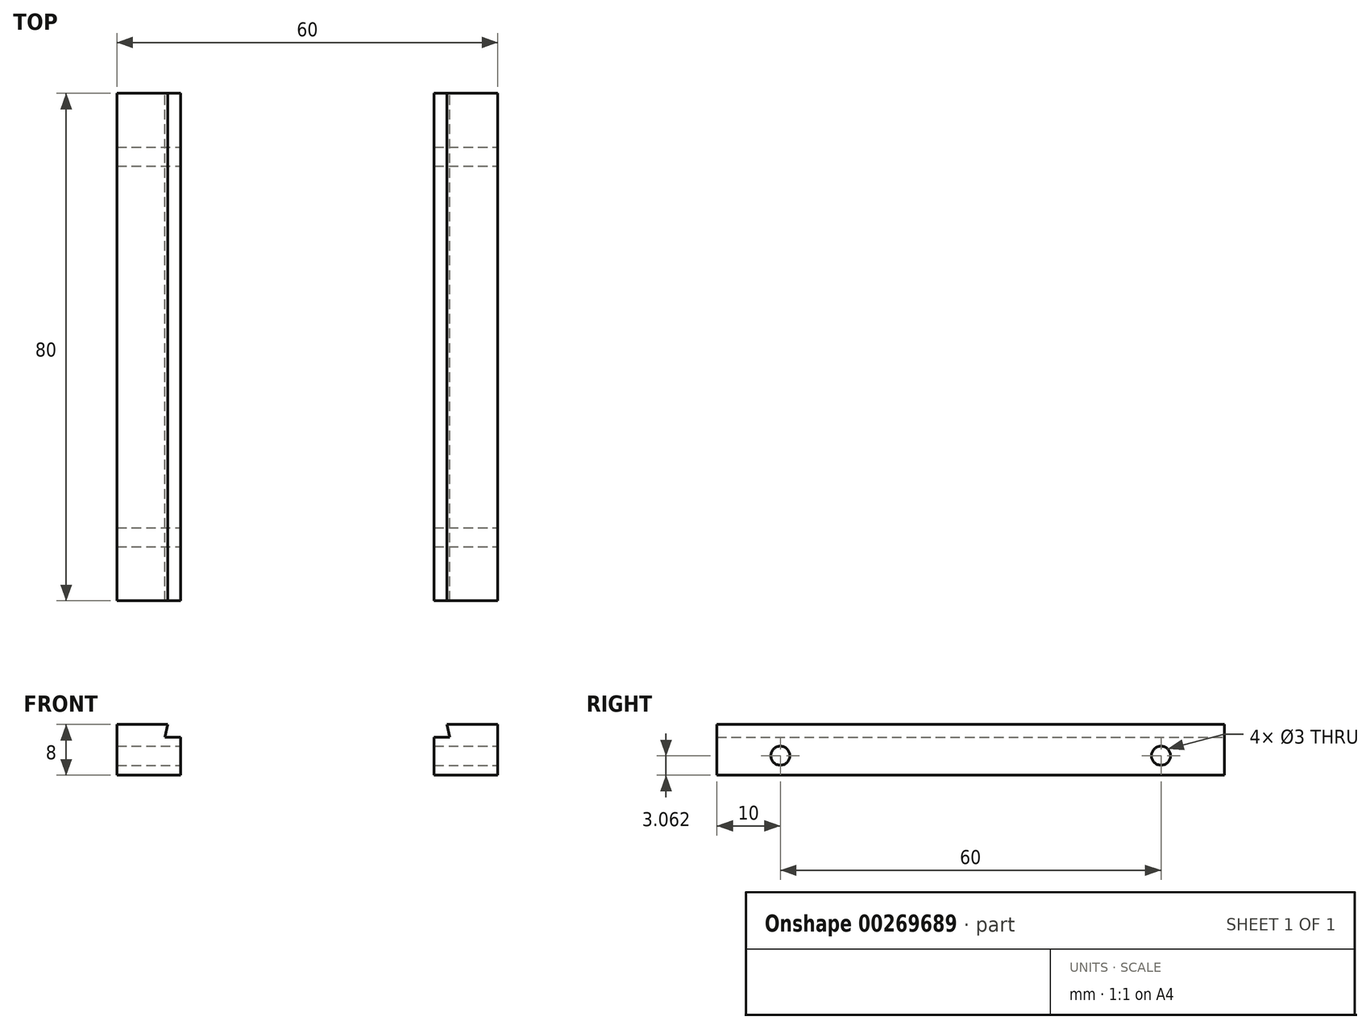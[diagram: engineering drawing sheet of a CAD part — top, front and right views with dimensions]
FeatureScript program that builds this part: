
annotation { "Feature Type Name" : "Feature", "Feature Type Description" : "" }
export const myFeature = defineFeature(function(context is Context, id is Id, definition is map)
    precondition{}
    {
        {
            var Q0;
            Q0=qCreatedBy(makeId("Front.planeOp"),FACE);
            var sketch = newSketch(context, id + "F0", { "sketchPlane" : qUnion([Q0])});
            skLineSegment(sketch, "E0.bottom", {"start": v(-30, 8) * mm, "end": v(-22, 8) * mm});
            skLineSegment(sketch, "E0.top", {"start": v(-30, 0) * mm, "end": v(-20, 0) * mm});
            skLineSegment(sketch, "E0.left", {"start": v(-30, 8) * mm, "end": v(-30, 0) * mm});
            skLineSegment(sketch, "E0.right", {"start": v(-20, 6) * mm, "end": v(-20, 0) * mm});
            skLineSegment(sketch, "E1", {"start": v(-22, 8) * mm, "end": v(-22.43, 6) * mm});
            skLineSegment(sketch, "E2", {"start": v(-22.43, 6) * mm, "end": v(-20, 6) * mm});
            skSolve(sketch);
        }
        {
            var Q0;
            Q0=makeQuery(id+"F0.imprint","IMPRINT",FACE,{"disambiguationData":[TD([[makeQuery(id+"F0.imprint","IMPRINT",EDGE,{"derivedFrom":sQuery(id+"F0.wireOp",EDGE,"E0.bottom")}),-1.0]])]});
            extrude(context, id + "F1", {"entities" : qUnion([Q0]), "depth" : 80 * mm});
        }
        {
            var Q0;
            Q0=makeQuery(id+"F1.opExtrude","SWEPT_BODY",BODY,{"disambiguationData":[OSD([sQuery(id+"F0.wireOp",EDGE,"E0.bottom"),sQuery(id+"F0.wireOp",EDGE,"E0.top"),sQuery(id+"F0.wireOp",EDGE,"E0.left"),sQuery(id+"F0.wireOp",EDGE,"E0.right"),sQuery(id+"F0.wireOp",EDGE,"E1"),sQuery(id+"F0.wireOp",EDGE,"E2")])]});
            var Q1;
            Q1=qCreatedBy(makeId("Right.planeOp"),FACE);
            mirror(context, id + "F2", {"entities" : qUnion([Q0]), "mirrorPlane" : qUnion([Q1])});
        }
        {
            var Q0;
            Q0=makeQuery(id+"F2.opPattern","COPY",FACE,{"derivedFrom":makeQuery(id+"F1.opExtrude","SWEPT_FACE",FACE,{"disambiguationData":[OSD([sQuery(id+"F0.wireOp",EDGE,"E0.left")])]}),"instanceName":"1"});
            var sketch = newSketch(context, id + "F3", { "sketchPlane" : qUnion([Q0])});
            skCircle(sketch, "E3", {"center": v(-70, 3.06) * mm, "radius": 1.5 * mm});
            skCircle(sketch, "E4", {"center": v(-10, 3.06) * mm, "radius": 1.5 * mm});
            skLineSegment(sketch, "E5", {"start": v(-80, 6.12) * mm, "end": v(0, 6.12) * mm, "construction": true});
            skLineSegment(sketch, "E6", {"start": v(-70, 3.06) * mm, "end": v(-70, 6.12) * mm, "construction": true});
            skLineSegment(sketch, "E7", {"start": v(-70, 3.06) * mm, "end": v(-70, 0) * mm, "construction": true});
            skLineSegment(sketch, "E8", {"start": v(-70, 3.06) * mm, "end": v(-80, 3.06) * mm, "construction": true});
            skLineSegment(sketch, "E9", {"start": v(-10, 3.06) * mm, "end": v(0, 3.06) * mm, "construction": true});
            skSolve(sketch);
        }
        {
            var Q0;
            Q0=makeQuery(id+"F3.imprint","IMPRINT",FACE,{"disambiguationData":[TD([[makeQuery(id+"F3.imprint","IMPRINT",EDGE,{"derivedFrom":sQuery(id+"F3.wireOp",EDGE,"E3")}),1.0]])]});
            var Q1;
            Q1=makeQuery(id+"F3.imprint","IMPRINT",FACE,{"disambiguationData":[TD([[makeQuery(id+"F3.imprint","IMPRINT",EDGE,{"derivedFrom":sQuery(id+"F3.wireOp",EDGE,"E4")}),1.0]])]});
            extrude(context, id + "F4", {"entities" : qUnion([Q0, Q1]), "operationType" : NewBodyOperationType.REMOVE, "oppositeDirection" : true, "depth" : 70 * mm});
        }
    });
